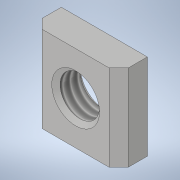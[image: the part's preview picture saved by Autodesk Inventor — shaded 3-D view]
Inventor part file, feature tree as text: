
AUTODESK INVENTOR PART (.ipt)
format: ipt  version: 2022 (Build 260153000, 153)  size: 131,584 bytes
history: native  units: mm
features: sketch x3, extrude x2, revolve x1, thread x1, plane x1
ambient origin geometry x8: Origin, YZ Plane, XZ Plane, XY Plane, X Axis, Y Axis, Z Axis, Center Point
bodies: Solid1 (feature_tree)
feature tree (8):
  extrude  "Extrusion1"  TaperAngle=360.0deg  [1 undecoded]
  revolve  "Revolution1"  [1 undecoded]
  thread  "Thread1"  [1 undecoded]
  extrude  "Extrusion2"  [1 undecoded]
  plane  "Work Plane1"
  sketch  "Sketch_1"  dims[d0=3.0mm d1=0.0mm d2=360.0deg]
  sketch  "Sketch_2"  dims[d3=2.134mm d4=0.0mm d5=18.0mm d6=0.0mm]
  sketch  "Sketch_3"
note: 4 required parameter values undecoded (feature->parameter linkage not recoverable at this tier; creation-order binding heuristic only, values carry confidence <= 0.55)